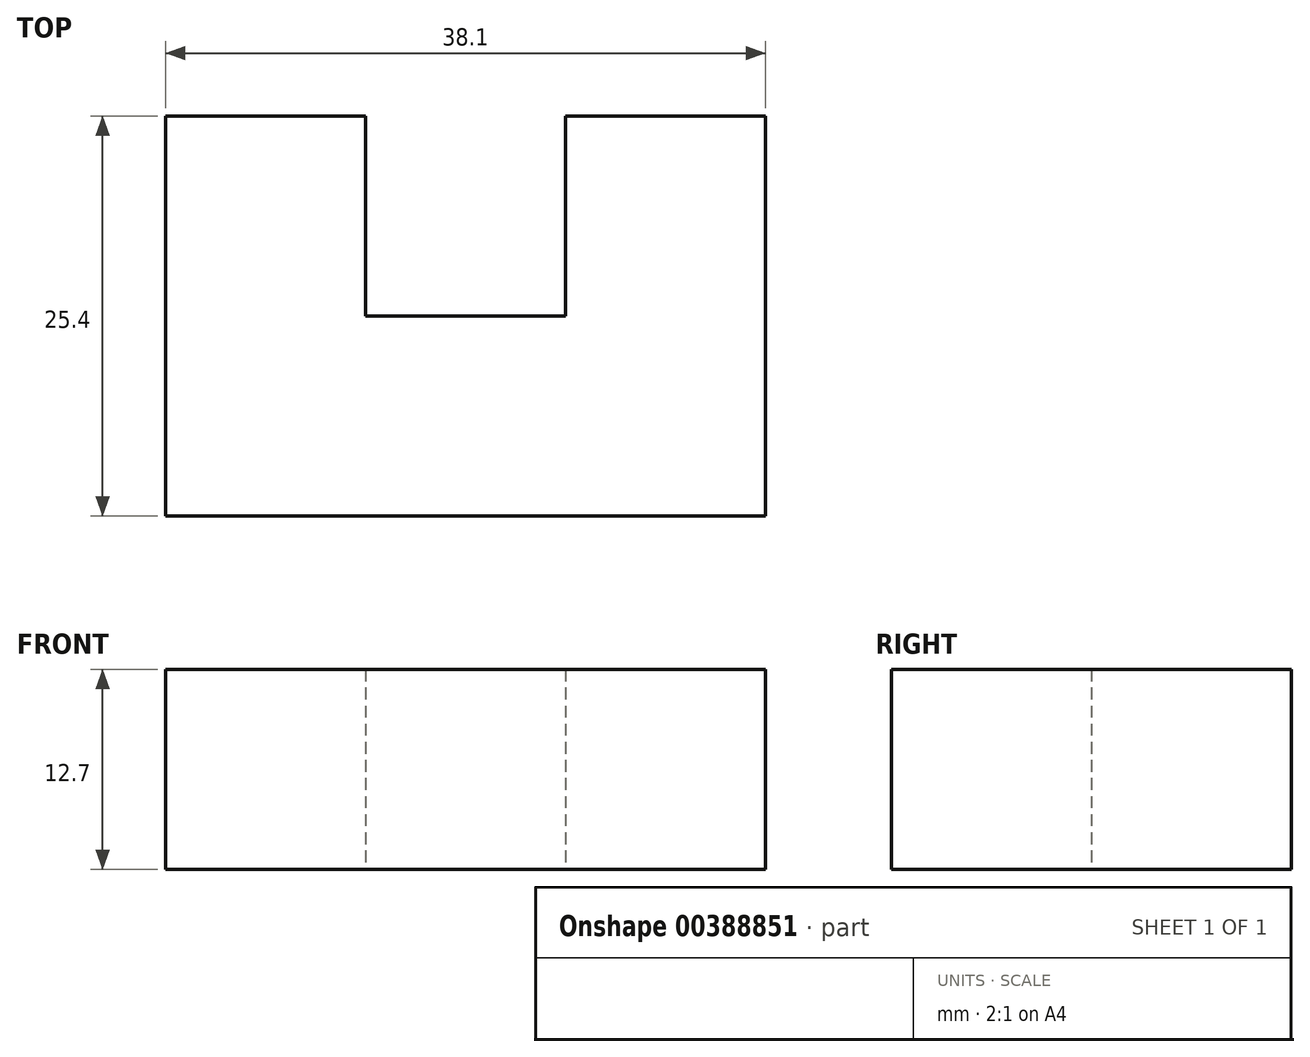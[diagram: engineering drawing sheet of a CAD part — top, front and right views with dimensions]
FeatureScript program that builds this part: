
annotation { "Feature Type Name" : "Feature", "Feature Type Description" : "" }
export const myFeature = defineFeature(function(context is Context, id is Id, definition is map)
    precondition{}
    {
        {
            var Q0;
            Q0=qCreatedBy(makeId("Top.planeOp"),FACE);
            var sketch = newSketch(context, id + "F0", { "sketchPlane" : qUnion([Q0])});
            skLineSegment(sketch, "E0.bottom", {"start": v(-25.4, 0) * mm, "end": v(12.7, 0) * mm});
            skLineSegment(sketch, "E0.top", {"start": v(-12.7, 12.7) * mm, "end": v(0, 12.7) * mm});
            skLineSegment(sketch, "E0.left", {"start": v(-25.4, 0) * mm, "end": v(-25.4, 12.7) * mm});
            skLineSegment(sketch, "E0.right", {"start": v(12.7, 0) * mm, "end": v(12.7, 12.7) * mm});
            skLineSegment(sketch, "E1.top", {"start": v(-25.4, 25.4) * mm, "end": v(-12.7, 25.4) * mm});
            skLineSegment(sketch, "E1.left", {"start": v(-25.4, 12.7) * mm, "end": v(-25.4, 25.4) * mm});
            skLineSegment(sketch, "E1.right", {"start": v(-12.7, 12.7) * mm, "end": v(-12.7, 25.4) * mm});
            skLineSegment(sketch, "E2.top", {"start": v(12.7, 25.4) * mm, "end": v(0, 25.4) * mm});
            skLineSegment(sketch, "E2.left", {"start": v(12.7, 12.7) * mm, "end": v(12.7, 25.4) * mm});
            skLineSegment(sketch, "E2.right", {"start": v(0, 12.7) * mm, "end": v(0, 25.4) * mm});
            skSolve(sketch);
        }
        {
            var Q0;
            Q0=makeQuery(id+"F0.imprint","IMPRINT",FACE,{"disambiguationData":[TD([[makeQuery(id+"F0.imprint","IMPRINT",EDGE,{"derivedFrom":sQuery(id+"F0.wireOp",EDGE,"E0.bottom")}),1.0]])]});
            extrude(context, id + "F1", {"entities" : qUnion([Q0]), "depth" : 12.7 * mm});
        }
    });
